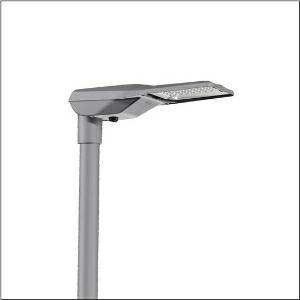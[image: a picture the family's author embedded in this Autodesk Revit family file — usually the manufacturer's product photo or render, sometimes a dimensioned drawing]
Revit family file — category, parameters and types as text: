
# Revit family: streetlight_sl_21_iq_mini___p0_8ab_5xe2r31u08hb_e37e
name_source: partatom
category: Lighting Fixtures
units: mm (PartAtom-declared; Revit-internal decimal feet)

## family parameters
Cut with Voids When Loaded = No
Host = Face
Light Source = No
Part Type = Normal
Room Calculation Point = No
Round Connector Dimension = Use Diameter
Shared = No

## types (1)
- --- (1 x LED, 8460 lm, 71 W, 3000K)
    Apparent Load = 71 VA
    CIE Flux Codes = 36 71 98 100 100
    Color Rendering = 70
    Color Temperature = 3000K
    Default Elevation = 1800 mm
    Description = Streetlight SL 21 iQ mini, mast luminaire, primary light control with lens, of PMMA, primary optical cover: cover, of toughened safety glass, transparent, light distribution: P0.8aB, light emission: direct distribution, primary light characteristic: asymmetric, installation type: post-top, side-entry, LED, High Power LED, rated luminous flux: 8.460lm, luminous efficacy: 119lm/W, light colour: 730, colour temperature: 3000K, control gear: iQ-Street Remote, D4i with power reduction, control: pre-setting: logarithmic dimming characteristic, Street-Remote, Auto-Match, Temp-Guard, Lumen-Switch, Night-Set, Smart-Wire, Light-Fading, Desk-Remote (wireless, voltage-free reading and setting of iQ features in the workshop via application-optimized NFC function/RFID function), optimised constant luminous flux control (CLO 2.0), mains connection: 220..240V, AC, 50/60Hz, start of lifetime: 71W, end of service life: 75W, reduction: 30W, luminaire housing, of diecast aluminium, powder-coated, SITECO metallic grey (DB 702S), corrosivity category C5 high according to DIN EN ISO 12944, please order mast flange separately, inclination adjustable: 0°, 5°, 10°, 15°, sealing non-destructively replaceable, multi-level sealing system, length: 628mm, width: 235mm, height: 110mm, mast flange for spigot size: 42mm (side-entry): 5XC10008XM4, 60/48mm (side-entry/post-top): 5XC10108XM2, 76/60mm (side-entry/post-top): 5XC10108XM1, mounting height: 4..8m, Smart Interface below, protection rating (complete): IP66, insulation class (complete): insulation class II (safety insulation), certification: CE, ENEC, ENEC+, VDE, impact resistance: IK10, permissible operating ambient temperature for outdoor applications: -40..+50°C, standard-compliant lighting for roads and squares, packaging unit: 1 piece

Light Distribution: P0.8aB
    Height = 110 mm
    Lamp = 1 x LED
    Lamp Light Flux = 8460 lm
    Lamp Power = 71 W
    Lamp count = 1
    Length = 625 mm
    Luminous efficacy = 119 lm/W
    Manufacturer = Siteco
    ModVariant = No
    Model = 5XE2R31U08HB
    Number of Poles = 1
    OnlyDefault = Yes
    Power Factor = 1
    Product Name = Streetlight SL 21 iQ mini | P0.8aB
    Product group = mast luminaire | pylon top
    ProductGroupID = 6100
    Protection Class = Protection class II
    Protection Degree = IP 66
    RLX_Detail_Level = 1
    RLX_Emergency_Light_Flux = 0 lm
    RLX_Emergency_Type = 0
    RLX_Emergency_Type_DB = No
    RlxData = <blob elided: 92081 chars, md5=843606bb>
    Socket = socket
    Standby Power = 0 W
    System Light Flux = 8460 lm
    System Power = 71 W
    Type Comments = factory setting: luminous flux: 100 % | dim-lin: 254 | 716 mA
    Type Image = l_1003516.jpg
    URL = http://relux.com
    VarID = @adj_083207
    Voltage = 0 V
    Weight = 0.00 kg
    Width = 234 mm

## geometry (parser evidence)
native form markers: Blend x4, Sweep x10
no freeform markers — native parametric forms only
